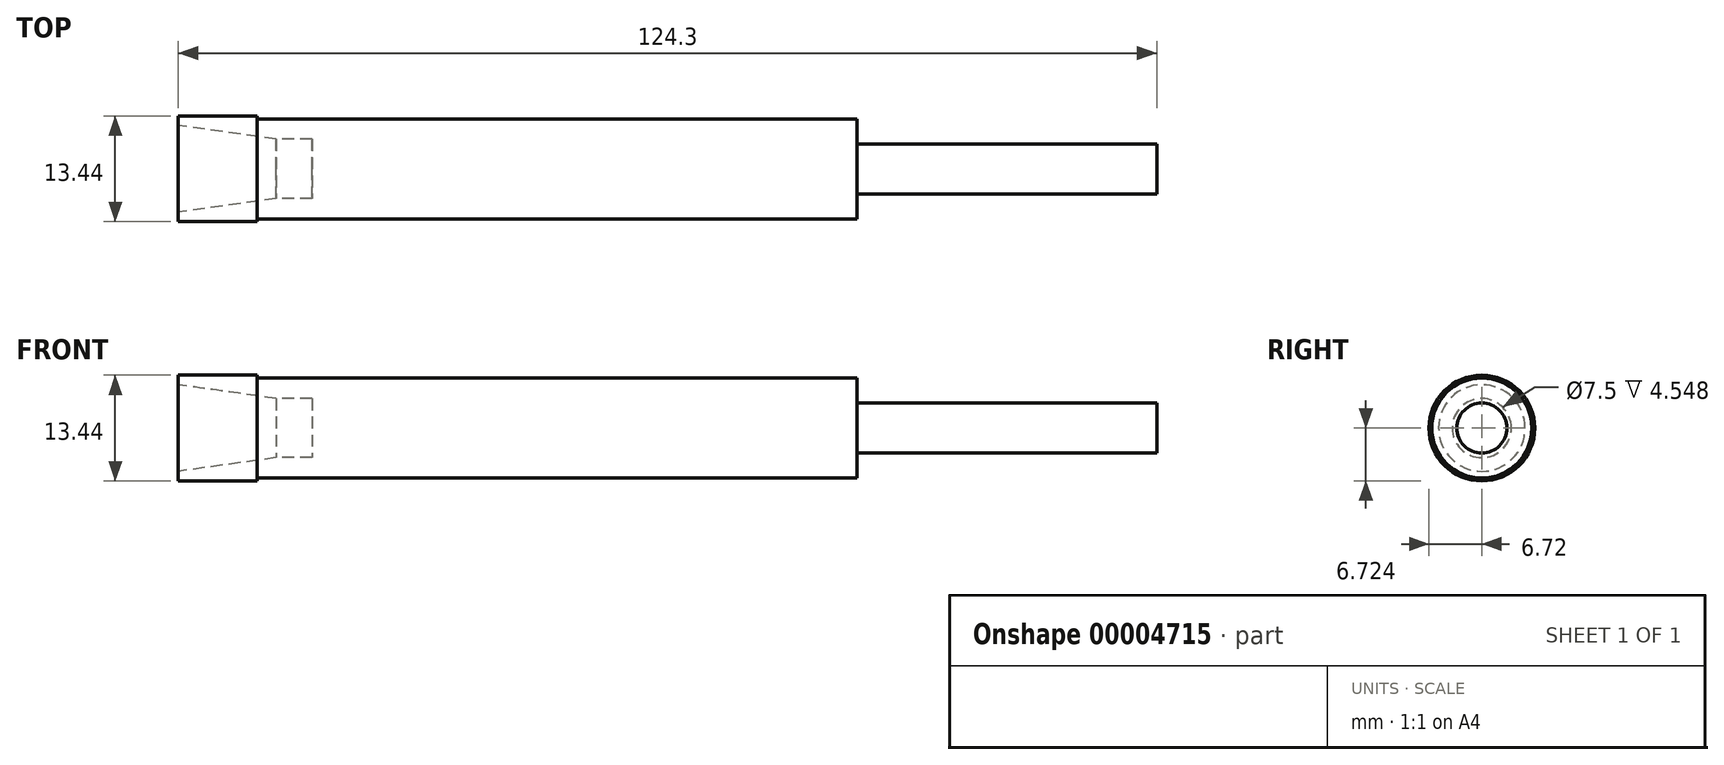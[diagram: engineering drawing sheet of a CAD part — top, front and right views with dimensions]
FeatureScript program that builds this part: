
annotation { "Feature Type Name" : "Feature", "Feature Type Description" : "" }
export const myFeature = defineFeature(function(context is Context, id is Id, definition is map)
    precondition{}
    {
        {
            var Q0;
            Q0=qCreatedBy(makeId("Front.planeOp"),FACE);
            var sketch = newSketch(context, id + "F0", { "sketchPlane" : qUnion([Q0])});
            skLineSegment(sketch, "E0", {"start": v(67.43, 3.29) * mm, "end": v(67.43, -3.06) * mm});
            skLineSegment(sketch, "E1", {"start": v(67.43, -3.06) * mm, "end": v(29.33, -3.06) * mm});
            skLineSegment(sketch, "E2", {"start": v(29.33, -3.06) * mm, "end": v(29.33, -6.24) * mm});
            skLineSegment(sketch, "E3", {"start": v(29.33, -6.24) * mm, "end": v(-46.87, -6.24) * mm});
            skLineSegment(sketch, "E4", {"start": v(-56.87, -6.6) * mm, "end": v(-56.87, -5.39) * mm});
            skLineSegment(sketch, "E5", {"start": v(-56.87, 6.83) * mm, "end": v(-46.87, 6.83) * mm});
            skLineSegment(sketch, "E6", {"start": v(29.33, 6.46) * mm, "end": v(29.33, 3.29) * mm});
            skLineSegment(sketch, "E7", {"start": v(29.33, 3.29) * mm, "end": v(67.43, 3.29) * mm});
            skLineSegment(sketch, "E8", {"start": v(-56.87, 5.61) * mm, "end": v(-56.87, 6.83) * mm});
            skLineSegment(sketch, "E9", {"start": v(-56.87, 5.61) * mm, "end": v(-44.42, 3.86) * mm});
            skLineSegment(sketch, "E10", {"start": v(-39.87, 3.86) * mm, "end": v(-39.87, -3.64) * mm});
            skLineSegment(sketch, "E11", {"start": v(-39.87, -3.64) * mm, "end": v(-44.42, -3.64) * mm});
            skLineSegment(sketch, "E12", {"start": v(-39.87, 0.11) * mm, "end": v(67.43, 0.11) * mm});
            skLineSegment(sketch, "E13", {"start": v(-44.42, 3.86) * mm, "end": v(-39.87, 3.86) * mm});
            skLineSegment(sketch, "E14", {"start": v(-44.42, -3.64) * mm, "end": v(-56.87, -5.39) * mm});
            skLineSegment(sketch, "E15", {"start": v(-46.87, 6.46) * mm, "end": v(-46.87, 6.83) * mm});
            skLineSegment(sketch, "E16", {"start": v(-46.87, 6.46) * mm, "end": v(29.33, 6.46) * mm});
            skLineSegment(sketch, "E17", {"start": v(-46.87, -6.6) * mm, "end": v(-56.87, -6.6) * mm});
            skLineSegment(sketch, "E18", {"start": v(-46.87, -6.6) * mm, "end": v(-46.87, -6.24) * mm});
            skSolve(sketch);
        }
        {
            var Q0;
            Q0=makeQuery(id+"F0.imprint","IMPRINT",FACE,{"disambiguationData":[TD([[makeQuery(id+"F0.imprint","IMPRINT",EDGE,{"derivedFrom":sQuery(id+"F0.wireOp",EDGE,"E5")}),-1.0]])]});
            var Q1;
            Q1=sQuery(id+"F0.wireOp",EDGE,"E12");
            revolve(context, id + "F1", {"entities" : qUnion([Q0]), "axis" : qUnion([Q1]), "revolveType" : RevolveType.FULL});
        }
    });
